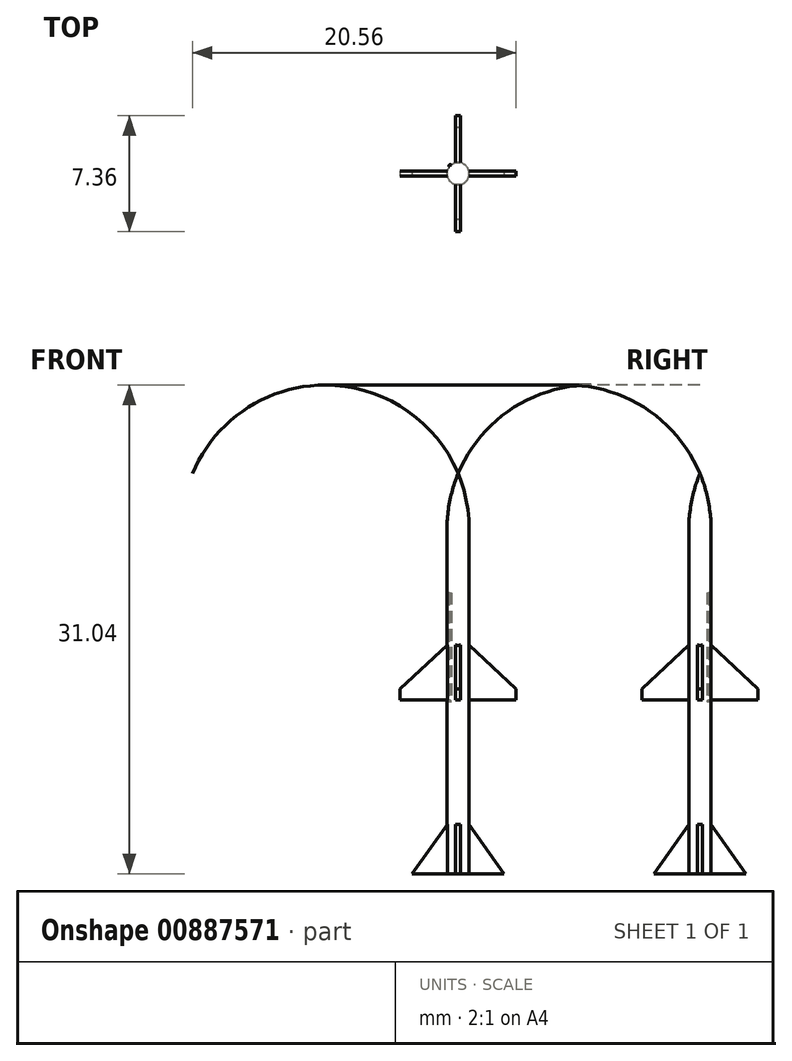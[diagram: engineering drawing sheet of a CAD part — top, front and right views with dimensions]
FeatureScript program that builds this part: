
annotation { "Feature Type Name" : "Feature", "Feature Type Description" : "" }
export const myFeature = defineFeature(function(context is Context, id is Id, definition is map)
    precondition{}
    {
        {
            var Q0;
            Q0=qCreatedBy(makeId("Front.planeOp"),FACE);
            var sketch = newSketch(context, id + "F0", { "sketchPlane" : qUnion([Q0])});
            skLineSegment(sketch, "E0", {"start": v(0, 0) * mm, "end": v(0, 25.42) * mm});
            skLineSegment(sketch, "E1", {"start": v(0.7, 21.9) * mm, "end": v(0.7, 0) * mm});
            skLineSegment(sketch, "E2", {"start": v(0.7, 0) * mm, "end": v(0, 0) * mm});
            skArc(sketch, "E3", {"start": v(0.7, 21.9) * mm, "mid": v(0.53, 23.7) * mm, "end": v(0, 25.42) * mm});
            skSolve(sketch);
        }
        {
            var Q0;
            Q0=makeQuery(id+"F0.imprint","IMPRINT",FACE,{"disambiguationData":[TD([[makeQuery(id+"F0.imprint","IMPRINT",EDGE,{"derivedFrom":sQuery(id+"F0.wireOp",EDGE,"E0")}),-1.0]])]});
            var Q1;
            Q1=sQuery(id+"F0.wireOp",EDGE,"E0");
            revolve(context, id + "F1", {"surfaceOperationType" : NewSurfaceOperationType.NEW, "entities" : qUnion([Q0]), "axis" : qUnion([Q1]), "revolveType" : RevolveType.FULL});
        }
        {
            var Q0;
            Q0=qCreatedBy(makeId("Front.planeOp"),FACE);
            var sketch = newSketch(context, id + "F2", { "sketchPlane" : qUnion([Q0])});
            skLineSegment(sketch, "E4", {"start": v(3.68, 11.04) * mm, "end": v(0.7, 11.04) * mm});
            skLineSegment(sketch, "E5", {"start": v(0.5, 3.4) * mm, "end": v(2.92, 0) * mm});
            skLineSegment(sketch, "E6", {"start": v(2.92, 0) * mm, "end": v(-2.92, 0) * mm});
            skLineSegment(sketch, "E7", {"start": v(-2.92, 0) * mm, "end": v(-0.5, 3.4) * mm});
            skLineSegment(sketch, "E8", {"start": v(-0.7, 11.04) * mm, "end": v(-3.68, 11.04) * mm});
            skLineSegment(sketch, "E9.0", {"start": v(0.7, 21.9) * mm, "end": v(-0.7, 21.9) * mm});
            skLineSegment(sketch, "E10", {"start": v(-3.68, 11.74) * mm, "end": v(-3.68, 11.04) * mm});
            skLineSegment(sketch, "E11", {"start": v(3.68, 11.04) * mm, "end": v(3.68, 11.74) * mm});
            skLineSegment(sketch, "E12", {"start": v(-0.34, 14.86) * mm, "end": v(-3.68, 11.74) * mm});
            skLineSegment(sketch, "E13", {"start": v(0.34, 14.86) * mm, "end": v(3.68, 11.74) * mm});
            skLineSegment(sketch, "E14", {"start": v(-0.5, 3.4) * mm, "end": v(0.5, 3.4) * mm});
            skLineSegment(sketch, "E15", {"start": v(-0.7, 11.04) * mm, "end": v(0.7, 11.04) * mm});
            skLineSegment(sketch, "E16.0", {"start": v(0.7, 0) * mm, "end": v(-0.7, 0) * mm});
            skLineSegment(sketch, "E17", {"start": v(0.7, 0) * mm, "end": v(0.7, 18.42) * mm, "construction": true});
            skPoint(sketch, "E18", {"position": v(0.7, 3.12) * mm});
            skLineSegment(sketch, "E19", {"start": v(-0.34, 14.86) * mm, "end": v(0.34, 14.86) * mm});
            skPoint(sketch, "E20", {"position": v(0.7, 14.51) * mm});
            skLineSegment(sketch, "E21", {"start": v(0, 21.9) * mm, "end": v(0, 11.04) * mm, "construction": true});
            skSolve(sketch);
        }
        {
            var Q0;
            Q0=makeQuery(id+"F2.imprint","IMPRINT",FACE,{"disambiguationData":[TD([[makeQuery(id+"F2.imprint","IMPRINT",EDGE,{"derivedFrom":sQuery(id+"F2.wireOp",EDGE,"RDLxK5Hz-ABav-6vcA-NfAG-7fdClgBCtLxT")}),-1.0]])]});
            var Q1;
            {var subQ3=sQuery(id+"F2.wireOp",EDGE,"E5");Q1=makeQuery(id+"F2.imprint","IMPRINT",FACE,{"disambiguationData":[TD([[makeQuery(id+"F2.imprint","IMPRINT",EDGE,{"derivedFrom":subQ3}),-1.0]])]});}
            var Q2;
            Q2=makeQuery(id+"F2.imprint","IMPRINT",FACE,{"disambiguationData":[TD([[makeQuery(id+"F2.imprint","IMPRINT",EDGE,{"derivedFrom":sQuery(id+"F2.wireOp",EDGE,"E4")}),-1.0]])]});
            extrude(context, id + "F3", {"entities" : qUnion([Q0, Q1, Q2]), "operationType" : NewBodyOperationType.ADD, "oppositeDirection" : true, "depth" : 0.3 * mm, "offsetDistance" : 25 * mm, "symmetric" : true});
        }
        {
            var Q0;
            Q0=makeQuery(id+"F1.opRevolve","SWEPT_BODY",BODY,{"disambiguationData":[OSD([sQuery(id+"F0.wireOp",EDGE,"E0"),sQuery(id+"F0.wireOp",EDGE,"E1"),sQuery(id+"F0.wireOp",EDGE,"E2"),sQuery(id+"F0.wireOp",EDGE,"E3")])]});
            var Q1;
            Q1=makeQuery(id+"F1.opRevolve","SWEPT_FACE",FACE,{"disambiguationData":[OSD([sQuery(id+"F0.wireOp",EDGE,"E1")])]});
            circularPattern(context, id + "F4", {"operationType" : NewBodyOperationType.ADD, "entities" : qUnion([Q0]), "axis" : qUnion([Q1]), "angle" : 360 * degree, "instanceCount" : 4, "equalSpace" : true, "computeTransformsWithoutBuiltin" : true});
        }
        {
            var Q0;
            {var subQ1=sQuery(id+"F2.wireOp",EDGE,"E15");var subQ4=sQuery(id+"F2.wireOp",EDGE,"E11");var subQ6=sQuery(id+"F2.wireOp",EDGE,"E8");var subQ7=sQuery(id+"F2.wireOp",EDGE,"E4");Q0=makeQuery(id+"F4.opPattern","COPY",FACE,{"derivedFrom":makeQuery(id+"F3.boolean.opBoolean","SPLIT",FACE,{"disambiguationData":[TD([makeQuery(id+"F3.opExtrude","SWEPT_FACE",FACE,{"disambiguationData":[OSD([subQ4])]})])],"derivedFrom":makeQuery(id+"F3.opExtrude","SWEPT_FACE",FACE,{"disambiguationData":[OSD([subQ7,subQ6,subQ1])]})}),"instanceName":"1"});}
            var sketch = newSketch(context, id + "F5", { "sketchPlane" : qUnion([Q0])});
            skCircle(sketch, "E22.1", {"center": v(0, 0) * mm, "radius": 0.7 * mm});
            skLineSegment(sketch, "E23.0.0", {"start": v(0, 0) * mm, "end": v(-0.51, 0) * mm, "construction": true});
            skLineSegment(sketch, "E24", {"start": v(-0.32, -0.44) * mm, "end": v(-0.44, -0.32) * mm});
            skLineSegment(sketch, "E25", {"start": v(-0.44, -0.32) * mm, "end": v(-0.55, -0.44) * mm});
            skLineSegment(sketch, "E26", {"start": v(-0.44, -0.55) * mm, "end": v(-0.32, -0.44) * mm});
            skLineSegment(sketch, "E27", {"start": v(0, 0) * mm, "end": v(-0.38, -0.38) * mm, "construction": true});
            skArc(sketch, "E28", {"start": v(-0.55, -0.44) * mm, "mid": v(-0.56, -0.56) * mm, "end": v(-0.44, -0.55) * mm});
            skSolve(sketch);
        }
        {
            var Q0;
            {var subQ0=sQuery(id+"F5.wireOp",EDGE,"E28");Q0=makeQuery(id+"F5.imprint","IMPRINT",FACE,{"disambiguationData":[TD([[makeQuery(id+"F5.imprint","IMPRINT",EDGE,{"derivedFrom":subQ0}),1.0]])]});}
            var Q1;
            {var subQ1=sQuery(id+"F5.wireOp",EDGE,"E25");Q1=makeQuery(id+"F5.imprint","IMPRINT",FACE,{"disambiguationData":[TD([[makeQuery(id+"F5.imprint","IMPRINT",EDGE,{"derivedFrom":subQ1}),1.0]])]});}
            extrude(context, id + "F6", {"entities" : qUnion([Q0, Q1]), "operationType" : NewBodyOperationType.ADD, "oppositeDirection" : true, "depth" : (965 / 144) * mm, "offsetDistance" : 25 * mm});
        }
        {
            var Q0;
            Q0=makeQuery(id+"F6.boolean.opBoolean","INTERSECT",EDGE,{"derivedFrom":[makeQuery(id+"F1SgjpEdBBOFuZJ_3.boolean.opBoolean","SPLIT",FACE,{"disambiguationData":[TD([makeQuery(id+"F1SgjpEdBBOFuZJ_3.opRevolve","SWEPT_FACE",FACE,{"disambiguationData":[OSD([sQuery(id+"FlY5MtBrKRYJxzp_3.wireOp",EDGE,"kaf6A2uF-OX8H-Va1Y-guTc-rQCtsMHh0R69")])]})])],"derivedFrom":makeQuery(id+"F1.opRevolve","SWEPT_FACE",FACE,{"disambiguationData":[OSD([sQuery(id+"F0.wireOp",EDGE,"E1")])]})}),makeQuery(id+"F6.opExtrude","CAP_FACE",FACE,{"disambiguationData":[OSD([sQuery(id+"F5.wireOp",EDGE,"E23.0.2"),sQuery(id+"F5.wireOp",EDGE,"E25"),sQuery(id+"F5.wireOp",EDGE,"E26"),sQuery(id+"F5.wireOp",EDGE,"E28")])],"isStart":false})]});
            var Q1;
            Q1=makeQuery(id+"F6.boolean.opBoolean","INTERSECT",EDGE,{"derivedFrom":[makeQuery(id+"F1SgjpEdBBOFuZJ_3.boolean.opBoolean","SPLIT",FACE,{"disambiguationData":[TD([makeQuery(id+"F1SgjpEdBBOFuZJ_3.opRevolve","SWEPT_FACE",FACE,{"disambiguationData":[OSD([sQuery(id+"FlY5MtBrKRYJxzp_3.wireOp",EDGE,"HS1JStHF-Ansh-H00f-Jenc-fMZRPMrZ2prO")])]})])],"derivedFrom":makeQuery(id+"F1.opRevolve","SWEPT_FACE",FACE,{"disambiguationData":[OSD([sQuery(id+"F0.wireOp",EDGE,"E1")])]})}),makeQuery(id+"F6.opExtrude","CAP_FACE",FACE,{"disambiguationData":[OSD([sQuery(id+"F5.wireOp",EDGE,"E23.0.2"),sQuery(id+"F5.wireOp",EDGE,"E25"),sQuery(id+"F5.wireOp",EDGE,"E26"),sQuery(id+"F5.wireOp",EDGE,"E28")])],"isStart":true})]});
            var Q2;
            Q2=makeQuery(id+"F8lxqWtCz5XsOnU_1.boolean.opBoolean","INTERSECT",EDGE,{"derivedFrom":[makeQuery(id+"F1SgjpEdBBOFuZJ_3.boolean.opBoolean","SPLIT",FACE,{"disambiguationData":[TD([makeQuery(id+"F1SgjpEdBBOFuZJ_3.opRevolve","SWEPT_FACE",FACE,{"disambiguationData":[OSD([sQuery(id+"FlY5MtBrKRYJxzp_3.wireOp",EDGE,"kaf6A2uF-OX8H-Va1Y-guTc-rQCtsMHh0R69")])]})])],"derivedFrom":makeQuery(id+"F1.opRevolve","SWEPT_FACE",FACE,{"disambiguationData":[OSD([sQuery(id+"F0.wireOp",EDGE,"E1")])]})}),makeQuery(id+"F8lxqWtCz5XsOnU_1.opExtrude","CAP_FACE",FACE,{"disambiguationData":[OSD([sQuery(id+"F0P3yee4YpAYUB5_1.wireOp",EDGE,"31262e74-cd09-43a4-a8cf-63d5588691cf.0.0"),sQuery(id+"F0P3yee4YpAYUB5_1.wireOp",EDGE,"TV5hKbbR-ihZ9-csuQ-lAUc-z30iWxt7CvSE"),sQuery(id+"F0P3yee4YpAYUB5_1.wireOp",EDGE,"XiSxz9GU-c4bM-KSi2-S3Hd-MBb2ZwAirnoL"),sQuery(id+"F0P3yee4YpAYUB5_1.wireOp",EDGE,"aPCBFern-o7FA-heLm-AFdk-XwTCuUbAZgXb")])],"isStart":false})]});
            chamfer(context, id + "F7", {"entities" : qUnion([Q0, Q1, Q2]), "width" : .1 * mm, "tangentPropagation" : true});
        }
    });
